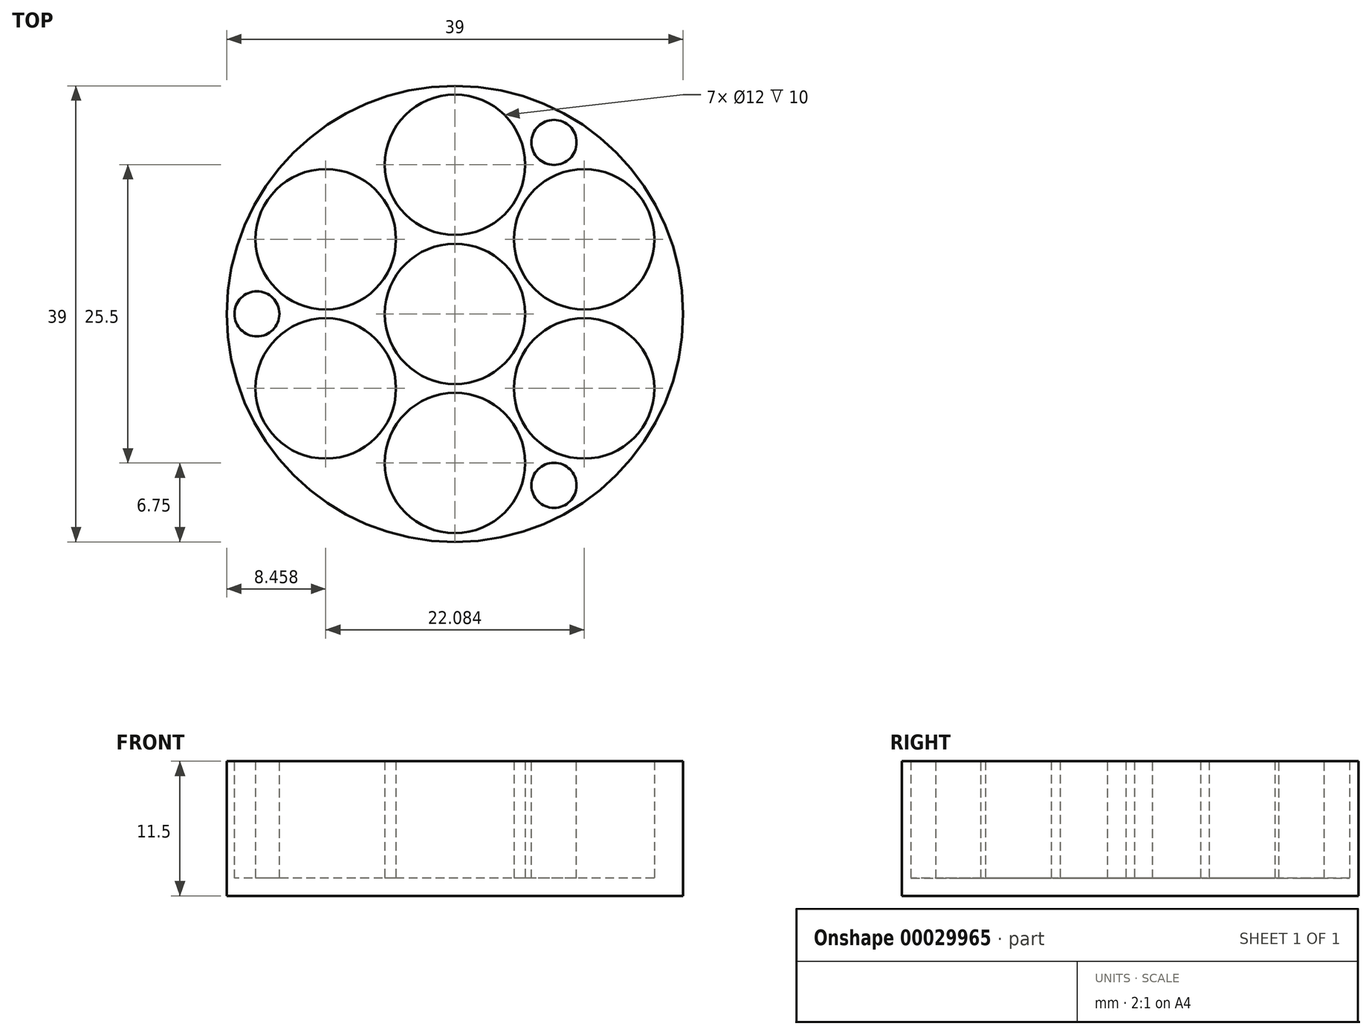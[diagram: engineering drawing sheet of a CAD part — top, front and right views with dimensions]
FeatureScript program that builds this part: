
annotation { "Feature Type Name" : "Feature", "Feature Type Description" : "" }
export const myFeature = defineFeature(function(context is Context, id is Id, definition is map)
    precondition{}
    {
        {
            var Q0;
            Q0=qCreatedBy(makeId("Top.planeOp"),FACE);
            var sketch = newSketch(context, id + "F0", { "sketchPlane" : qUnion([Q0])});
            skCircle(sketch, "E0", {"center": v(0, 0) * mm, "radius": 19.5 * mm});
            skSolve(sketch);
        }
        {
            var Q0;
            Q0 = qSketchRegion(id + "F0", true);
            extrude(context, id + "F1", {"entities" : qUnion([Q0]), "depth" : 1.5 * mm});
        }
        {
            var Q0;
            Q0=makeQuery(id+"F1.opExtrude","CAP_FACE",FACE,{"disambiguationData":[OSD([sQuery(id+"F0.wireOp",EDGE,"E0")])],"isStart":false});
            var sketch = newSketch(context, id + "F2", { "sketchPlane" : qUnion([Q0])});
            skCircle(sketch, "E1", {"center": v(0, 0) * mm, "radius": 19.5 * mm});
            skCircle(sketch, "E2", {"center": v(0, 0) * mm, "radius": 6 * mm});
            skLineSegment(sketch, "E3", {"start": v(0, 6) * mm, "end": v(0, 19.5) * mm});
            skCircle(sketch, "E4", {"center": v(0, 12.75) * mm, "radius": 6 * mm});
            skCircle(sketch, "E5.1.0", {"center": v(-11.04, 6.38) * mm, "radius": 6 * mm});
            skCircle(sketch, "E5.2.0", {"center": v(-11.04, -6.37) * mm, "radius": 6 * mm});
            skCircle(sketch, "E5.3.0", {"center": v(0, -12.75) * mm, "radius": 6 * mm});
            skCircle(sketch, "E5.4.0", {"center": v(11.04, -6.38) * mm, "radius": 6 * mm});
            skCircle(sketch, "E5.5.0", {"center": v(11.04, 6.38) * mm, "radius": 6 * mm});
            skSolve(sketch);
        }
        {
            var Q0;
            Q0=makeQuery(id+"F2.imprint","IMPRINT",FACE,{"disambiguationData":[TD([[makeQuery(id+"F2.imprint","IMPRINT",EDGE,{"derivedFrom":sQuery(id+"F2.wireOp",EDGE,"E1")}),1.0]])]});
            extrude(context, id + "F3", {"entities" : qUnion([Q0]), "operationType" : NewBodyOperationType.ADD, "depth" : 10 * mm});
        }
        {
            var Q0;
            Q0=makeQuery(id+"F3.opExtrude","CAP_FACE",FACE,{"disambiguationData":[OSD([sQuery(id+"F2.wireOp",EDGE,"E1"),sQuery(id+"F2.wireOp",EDGE,"E2"),sQuery(id+"F2.wireOp",EDGE,"E4"),sQuery(id+"F2.wireOp",EDGE,"E5.1.0"),sQuery(id+"F2.wireOp",EDGE,"E5.2.0"),sQuery(id+"F2.wireOp",EDGE,"E5.3.0"),sQuery(id+"F2.wireOp",EDGE,"E5.4.0"),sQuery(id+"F2.wireOp",EDGE,"E5.5.0")])],"isStart":false});
            var sketch = newSketch(context, id + "F4", { "sketchPlane" : qUnion([Q0])});
            skCircle(sketch, "E6", {"center": v(-16.93, 0) * mm, "radius": 1.93 * mm});
            skCircle(sketch, "E7.1.0", {"center": v(8.46, -14.66) * mm, "radius": 1.93 * mm});
            skCircle(sketch, "E7.2.0", {"center": v(8.46, 14.66) * mm, "radius": 1.93 * mm});
            skPoint(sketch, "E7.center", {"position": v(0, 0) * mm});
            skSolve(sketch);
        }
        {
            var Q0;
            Q0 = qSketchRegion(id + "F4", true);
            extrude(context, id + "F5", {"entities" : qUnion([Q0]), "operationType" : NewBodyOperationType.REMOVE, "oppositeDirection" : true, "depth" : 10 * mm});
        }
    });
